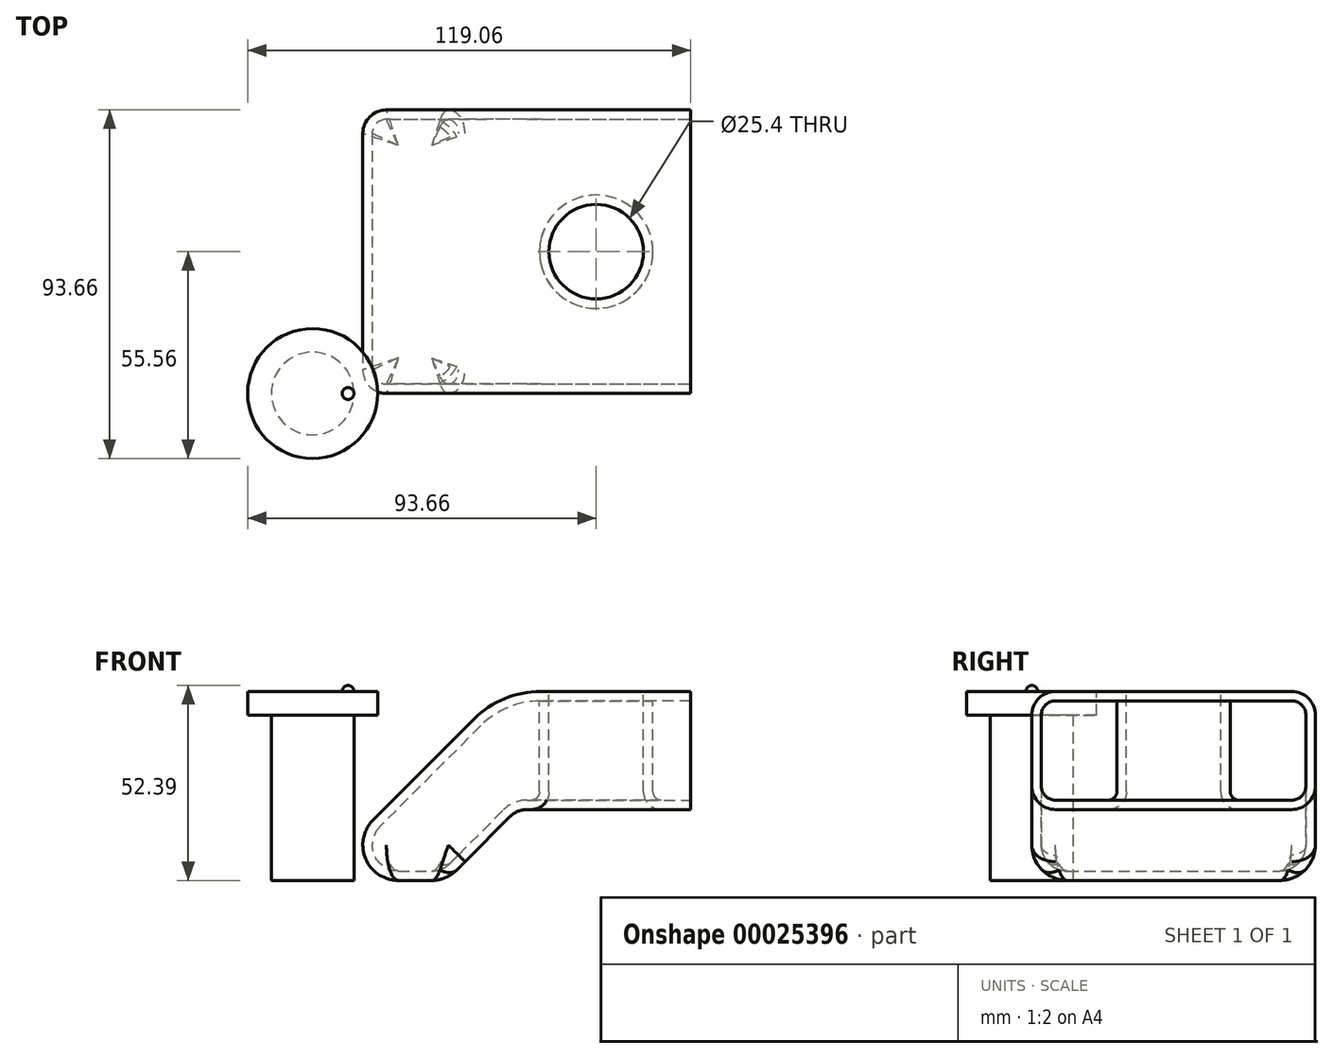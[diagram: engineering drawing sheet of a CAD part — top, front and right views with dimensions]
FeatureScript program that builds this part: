
annotation { "Feature Type Name" : "Feature", "Feature Type Description" : "" }
export const myFeature = defineFeature(function(context is Context, id is Id, definition is map)
    precondition{}
    {
        {
            var Q0;
            Q0=qCreatedBy(makeId("Front.planeOp"),FACE);
            var sketch = newSketch(context, id + "F0", { "sketchPlane" : qUnion([Q0])});
            skLineSegment(sketch, "E0", {"start": v(0, 0) * mm, "end": v(50.8, 50.8) * mm});
            skLineSegment(sketch, "E1", {"start": v(50.8, 50.8) * mm, "end": v(101.6, 50.8) * mm});
            skLineSegment(sketch, "E2", {"start": v(101.6, 50.8) * mm, "end": v(101.6, 19.05) * mm});
            skLineSegment(sketch, "E3", {"start": v(101.6, 19.05) * mm, "end": v(54.97, 19.05) * mm});
            skLineSegment(sketch, "E4", {"start": v(54.97, 19.05) * mm, "end": v(35.92, 0) * mm});
            skLineSegment(sketch, "E5", {"start": v(35.92, 0) * mm, "end": v(0, 0) * mm});
            skSolve(sketch);
        }
        {
            var Q0;
            Q0 = qSketchRegion(id + "F0", true);
            extrude(context, id + "F1", {"entities" : qUnion([Q0]), "oppositeDirection" : true, "depth" : 76.2 * mm});
        }
        {
            var Q0;
            Q0=makeQuery(id+"F1.opExtrude","SWEPT_FACE",FACE,{"disambiguationData":[OSD([sQuery(id+"F0.wireOp",EDGE,"E1")])]});
            var sketch = newSketch(context, id + "F2", { "sketchPlane" : qUnion([Q0])});
            skLineSegment(sketch, "E6", {"start": v(50.8, 76.2) * mm, "end": v(101.6, 0) * mm, "construction": true});
            skCircle(sketch, "E7", {"center": v(76.2, 38.1) * mm, "radius": 12.7 * mm});
            skSolve(sketch);
        }
        {
            var Q0;
            Q0 = qSketchRegion(id + "F2", true);
            extrude(context, id + "F3", {"entities" : qUnion([Q0]), "operationType" : NewBodyOperationType.REMOVE, "endBound" : BoundingType.THROUGH_ALL, "oppositeDirection" : true, "depth" : 25.4 * mm});
        }
        {
            var Q0;
            Q0=makeQuery(id+"F1.opExtrude","SWEPT_EDGE",EDGE,{"disambiguationData":[OSD([sQuery(id+"F0.wireOp",EDGE,"E0"),sQuery(id+"F0.wireOp",EDGE,"E1")])]});
            fillet(context, id + "F4", {"entities" : qUnion([Q0]), "radius" : 25.4 * mm, "tangentPropagation" : true, "allowEdgeOverflow" : false});
        }
        {
            var Q0;
            Q0=makeQuery(id+"F1.opExtrude","SWEPT_EDGE",EDGE,{"disambiguationData":[OSD([sQuery(id+"F0.wireOp",EDGE,"E3"),sQuery(id+"F0.wireOp",EDGE,"E4")])]});
            fillet(context, id + "F5", {"entities" : qUnion([Q0]), "radius" : 6.35 * mm, "tangentPropagation" : true, "allowEdgeOverflow" : false});
        }
        {
            var Q0;
            Q0=makeQuery(id+"F1.opExtrude","CAP_EDGE",EDGE,{"disambiguationData":[OSD([sQuery(id+"F0.wireOp",EDGE,"E1")])],"isStart":true});
            var Q1;
            Q1=makeQuery(id+"F1.opExtrude","CAP_EDGE",EDGE,{"disambiguationData":[OSD([sQuery(id+"F0.wireOp",EDGE,"E1")])],"isStart":false});
            var Q2;
            Q2=makeQuery(id+"F1.opExtrude","CAP_EDGE",EDGE,{"disambiguationData":[OSD([sQuery(id+"F0.wireOp",EDGE,"E3")])],"isStart":false});
            var Q3;
            Q3=makeQuery(id+"F1.opExtrude","CAP_EDGE",EDGE,{"disambiguationData":[OSD([sQuery(id+"F0.wireOp",EDGE,"E3")])],"isStart":true});
            fillet(context, id + "F6", {"entities" : qUnion([Q0, Q1, Q2, Q3]), "radius" : 6.35 * mm, "tangentPropagation" : true, "allowEdgeOverflow" : false});
        }
        {
            var Q0;
            Q0=makeQuery(id+"F3.boolean.opBoolean","COPY",EDGE,{"derivedFrom":makeQuery(id+"F3.opExtrude","CAP_EDGE",EDGE,{"disambiguationData":[OSD([sQuery(id+"F2.wireOp",EDGE,"E7")])],"isStart":true})});
            var Q1;
            Q1=makeQuery(id+"F3.boolean.opBoolean","INTERSECT",EDGE,{"derivedFrom":[makeQuery(id+"F1.opExtrude","SWEPT_FACE",FACE,{"disambiguationData":[OSD([sQuery(id+"F0.wireOp",EDGE,"E3")])]}),makeQuery(id+"F3.opExtrude","SWEPT_FACE",FACE,{"disambiguationData":[OSD([sQuery(id+"F2.wireOp",EDGE,"E7")])]})]});
            fillet(context, id + "F7", {"entities" : qUnion([Q0, Q1]), "radius" : 4.78 * mm, "tangentPropagation" : true, "allowEdgeOverflow" : false});
        }
        {
            var Q0;
            Q0=makeQuery(id+"F1.opExtrude","SWEPT_EDGE",EDGE,{"disambiguationData":[OSD([sQuery(id+"F0.wireOp",EDGE,"E4"),sQuery(id+"F0.wireOp",EDGE,"E5")])]});
            fillet(context, id + "F8", {"entities" : qUnion([Q0]), "radius" : 9.52 * mm, "tangentPropagation" : true, "allowEdgeOverflow" : false});
        }
        {
            var Q0;
            Q0=makeQuery(id+"F1.opExtrude","SWEPT_FACE",FACE,{"disambiguationData":[OSD([sQuery(id+"F0.wireOp",EDGE,"E2")])]});
            shell(context, id + "F9", {"entities" : qUnion([Q0]), "thickness" : 2.54 * mm});
        }
        {
            var Q0;
            Q0=qCreatedBy(makeId("Top.planeOp"),FACE);
            var sketch = newSketch(context, id + "F10", { "sketchPlane" : qUnion([Q0])});
            skCircle(sketch, "E8", {"center": v(0, 0) * mm, "radius": 11.11 * mm});
            skSolve(sketch);
        }
        {
            var Q0;
            Q0 = qSketchRegion(id + "F10", true);
            extrude(context, id + "F11", {"entities" : qUnion([Q0]), "depth" : 50.8 * mm});
        }
        {
            var Q0;
            Q0=makeQuery(id+"F11.opExtrude","CAP_FACE",FACE,{"disambiguationData":[OSD([sQuery(id+"F10.wireOp",EDGE,"E8")])],"isStart":false});
            var sketch = newSketch(context, id + "F12", { "sketchPlane" : qUnion([Q0])});
            skCircle(sketch, "E9.0", {"center": v(0, 0) * mm, "radius": 17.46 * mm});
            skSolve(sketch);
        }
        {
            var Q0;
            Q0 = qSketchRegion(id + "F12", true);
            extrude(context, id + "F13", {"entities" : qUnion([Q0]), "operationType" : NewBodyOperationType.ADD, "oppositeDirection" : true, "depth" : 6.35 * mm});
        }
        {
            var Q0;
            Q0=makeQuery(id+"F13.boolean.opBoolean","MERGE",FACE,{"derivedFrom":[makeQuery(id+"F11.opExtrude","CAP_FACE",FACE,{"disambiguationData":[OSD([sQuery(id+"F10.wireOp",EDGE,"E8")])],"isStart":false}),makeQuery(id+"F13.opExtrude","CAP_FACE",FACE,{"disambiguationData":[OSD([sQuery(id+"F12.wireOp",EDGE,"E9.0")])],"isStart":true})]});
            var sketch = newSketch(context, id + "F14", { "sketchPlane" : qUnion([Q0])});
            skLineSegment(sketch, "E10", {"start": v(0, 0) * mm, "end": v(17.46, 0) * mm, "construction": true});
            skArc(sketch, "E11", {"start": v(11.11, 0) * mm, "mid": v(9.53, 1.59) * mm, "end": v(7.94, 0) * mm});
            skCircle(sketch, "E12.0", {"center": v(0, 0) * mm, "radius": 17.46 * mm, "construction": true});
            skLineSegment(sketch, "E13", {"start": v(7.94, 0) * mm, "end": v(11.11, 0) * mm});
            skSolve(sketch);
        }
        {
            var Q0;
            Q0 = qSketchRegion(id + "F14", true);
            var Q1;
            Q1=sQuery(id+"F14.wireOp",EDGE,"E10");
            revolve(context, id + "F15", {"operationType" : NewBodyOperationType.ADD, "entities" : qUnion([Q0]), "axis" : qUnion([Q1]), "revolveType" : RevolveType.ONE_DIRECTION, "angle" : 180 * degree});
        }
    });
